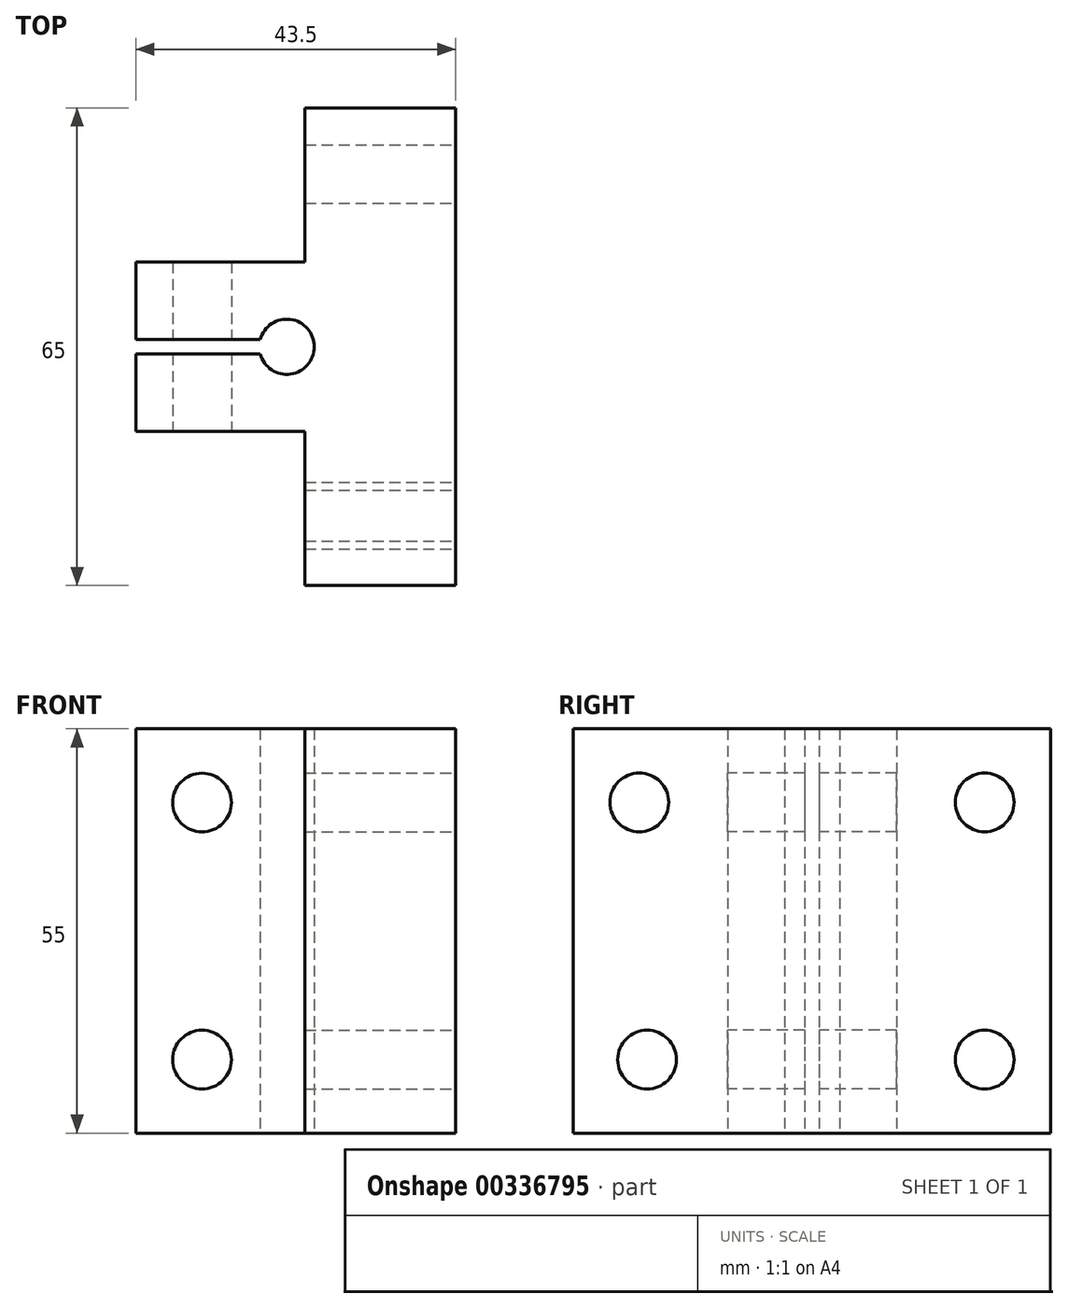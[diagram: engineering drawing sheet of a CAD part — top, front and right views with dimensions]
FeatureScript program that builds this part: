
annotation { "Feature Type Name" : "Feature", "Feature Type Description" : "" }
export const myFeature = defineFeature(function(context is Context, id is Id, definition is map)
    precondition{}
    {
        {
            var Q0;
            Q0=qCreatedBy(makeId("Top.planeOp"),FACE);
            var sketch = newSketch(context, id + "F0", { "sketchPlane" : qUnion([Q0])});
            skLineSegment(sketch, "E0", {"start": v(51.87, 33.5) * mm, "end": v(51.87, -31.5) * mm});
            skLineSegment(sketch, "E1", {"start": v(51.87, 33.5) * mm, "end": v(31.37, 33.5) * mm});
            skLineSegment(sketch, "E2", {"start": v(51.87, -31.5) * mm, "end": v(31.37, -31.5) * mm});
            skLineSegment(sketch, "E3", {"start": v(31.37, -31.5) * mm, "end": v(31.37, -10.5) * mm});
            skLineSegment(sketch, "E4", {"start": v(31.37, 33.5) * mm, "end": v(31.37, 12.5) * mm});
            skLineSegment(sketch, "E5", {"start": v(31.37, 12.5) * mm, "end": v(8.37, 12.5) * mm});
            skLineSegment(sketch, "E6", {"start": v(31.37, -10.5) * mm, "end": v(8.37, -10.5) * mm});
            skLineSegment(sketch, "E7", {"start": v(8.37, -10.5) * mm, "end": v(8.37, 0) * mm});
            skLineSegment(sketch, "E8", {"start": v(8.37, 12.5) * mm, "end": v(8.37, 2) * mm});
            skArc(sketch, "E9", {"start": v(25.29, 0) * mm, "mid": v(32.65, 1) * mm, "end": v(25.29, 2) * mm});
            skLineSegment(sketch, "E10", {"start": v(8.37, 0) * mm, "end": v(25.29, 0) * mm});
            skLineSegment(sketch, "E11", {"start": v(8.37, 2) * mm, "end": v(25.29, 2) * mm});
            skPoint(sketch, "E12.orphan", {"position": v(31.37, 1) * mm});
            skPoint(sketch, "E13.start.orphan", {"position": v(51.87, 1) * mm});
            skSolve(sketch);
        }
        {
            var Q0;
            Q0=makeQuery(id+"F0.imprint","IMPRINT",FACE,{"disambiguationData":[TD([[makeQuery(id+"F0.imprint","IMPRINT",EDGE,{"derivedFrom":sQuery(id+"F0.wireOp",EDGE,"E0")}),-1.0]])]});
            extrude(context, id + "F1", {"entities" : qUnion([Q0]), "depth" : 55 * mm});
        }
        {
            var Q0;
            Q0=makeQuery(id+"F1.opExtrude","SWEPT_FACE",FACE,{"disambiguationData":[OSD([sQuery(id+"F0.wireOp",EDGE,"E6")])]});
            var sketch = newSketch(context, id + "F2", { "sketchPlane" : qUnion([Q0])});
            skLineSegment(sketch, "E14", {"start": v(8.37, 55) * mm, "end": v(17.37, 55) * mm});
            skLineSegment(sketch, "E15", {"start": v(8.37, 55) * mm, "end": v(8.37, 44.98) * mm});
            skLineSegment(sketch, "E16", {"start": v(8.37, 44.98) * mm, "end": v(17.37, 44.98) * mm});
            skCircle(sketch, "E17", {"center": v(17.37, 44.98) * mm, "radius": 4 * mm});
            skLineSegment(sketch, "E18", {"start": v(8.37, 0) * mm, "end": v(17.37, 0) * mm});
            skLineSegment(sketch, "E19", {"start": v(8.37, 0) * mm, "end": v(8.37, 10) * mm});
            skLineSegment(sketch, "E20", {"start": v(8.37, 10) * mm, "end": v(17.37, 10) * mm});
            skCircle(sketch, "E21", {"center": v(17.37, 10) * mm, "radius": 4 * mm});
            skSolve(sketch);
        }
        {
            var Q0;
            Q0 = qSketchRegion(id + "F2", true);
            extrude(context, id + "F3", {"entities" : qUnion([Q0]), "operationType" : NewBodyOperationType.REMOVE, "endBound" : BoundingType.THROUGH_ALL, "oppositeDirection" : true, "depth" : 25 * mm});
        }
        {
            var Q0;
            Q0=makeQuery(id+"F1.opExtrude","SWEPT_FACE",FACE,{"disambiguationData":[OSD([sQuery(id+"F0.wireOp",EDGE,"E0")])]});
            var sketch = newSketch(context, id + "F4", { "sketchPlane" : qUnion([Q0])});
            skLineSegment(sketch, "E22", {"start": v(-31.5, 0) * mm, "end": v(-31.5, 10) * mm});
            skLineSegment(sketch, "E23", {"start": v(-31.5, 55) * mm, "end": v(-31.5, 45) * mm});
            skLineSegment(sketch, "E24", {"start": v(33.5, 55) * mm, "end": v(33.5, 45) * mm});
            skLineSegment(sketch, "E25", {"start": v(33.5, 0) * mm, "end": v(33.5, 10) * mm});
            skLineSegment(sketch, "E26", {"start": v(-31.5, 55) * mm, "end": v(-22.5, 55) * mm});
            skLineSegment(sketch, "E27", {"start": v(33.5, 55) * mm, "end": v(24.5, 55) * mm});
            skLineSegment(sketch, "E28", {"start": v(33.5, 0) * mm, "end": v(24.5, 0) * mm});
            skLineSegment(sketch, "E29", {"start": v(-31.5, 0) * mm, "end": v(-21.44, 0) * mm});
            skLineSegment(sketch, "E30", {"start": v(-31.5, 10) * mm, "end": v(-21.44, 10) * mm});
            skLineSegment(sketch, "E31", {"start": v(-31.5, 45) * mm, "end": v(-22.5, 45) * mm});
            skLineSegment(sketch, "E32", {"start": v(33.5, 45) * mm, "end": v(24.5, 45) * mm});
            skLineSegment(sketch, "E33", {"start": v(33.5, 10) * mm, "end": v(24.5, 10) * mm});
            skCircle(sketch, "E34", {"center": v(-22.5, 45) * mm, "radius": 4 * mm});
            skCircle(sketch, "E35", {"center": v(24.5, 45) * mm, "radius": 4 * mm});
            skCircle(sketch, "E36", {"center": v(24.5, 10) * mm, "radius": 4 * mm});
            skCircle(sketch, "E37", {"center": v(-21.44, 10) * mm, "radius": 4 * mm});
            skSolve(sketch);
        }
        {
            var Q0;
            Q0 = qSketchRegion(id + "F4", true);
            extrude(context, id + "F5", {"entities" : qUnion([Q0]), "operationType" : NewBodyOperationType.REMOVE, "endBound" : BoundingType.THROUGH_ALL, "oppositeDirection" : true, "depth" : 25 * mm});
        }
    });
